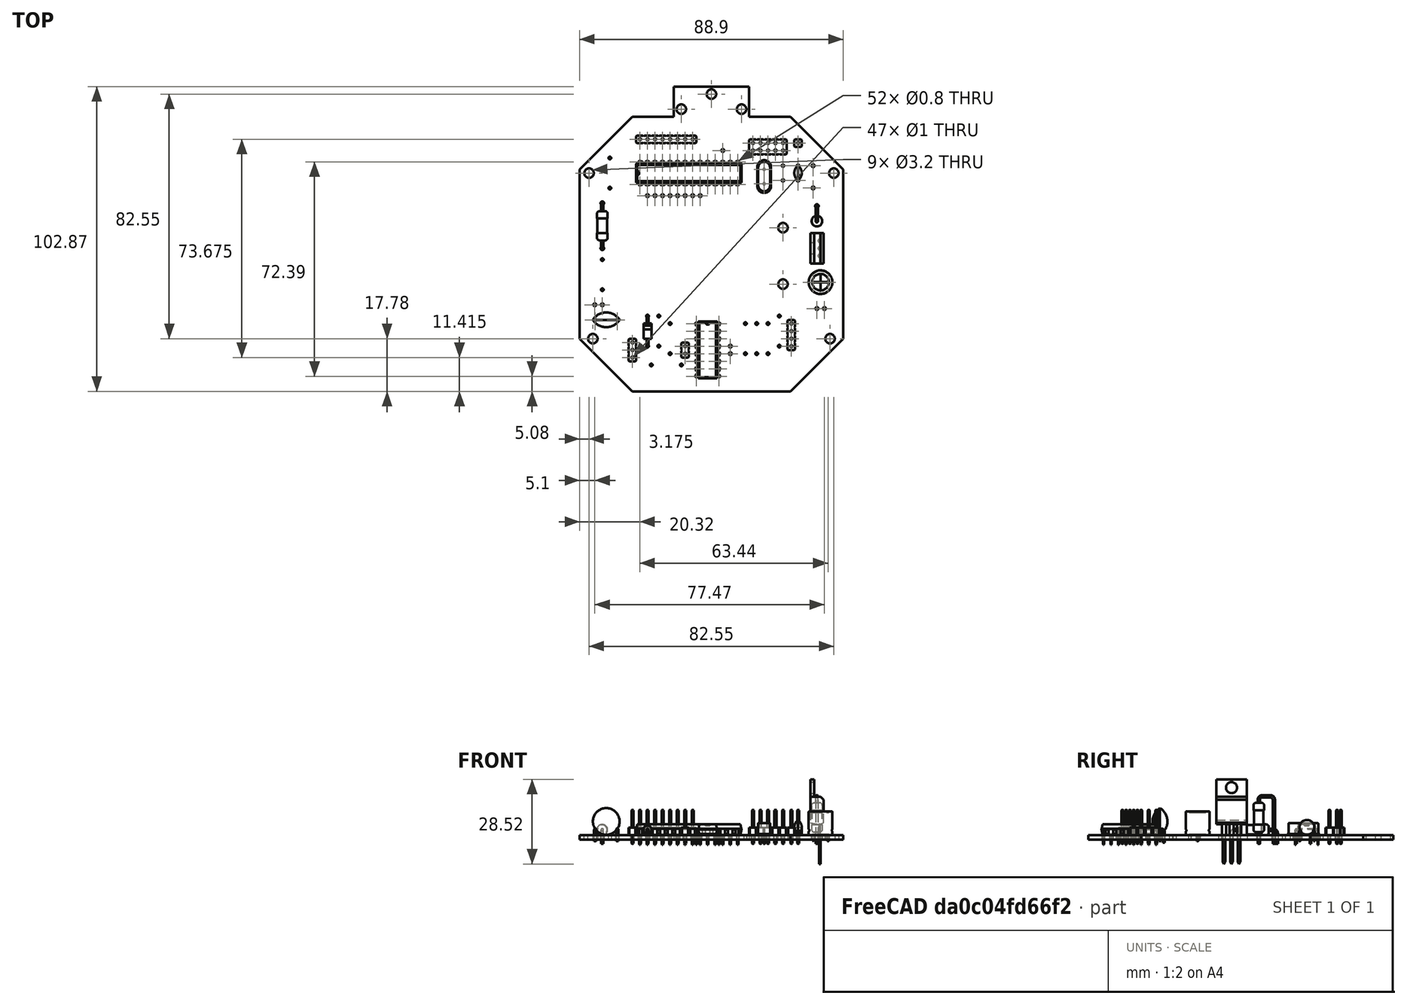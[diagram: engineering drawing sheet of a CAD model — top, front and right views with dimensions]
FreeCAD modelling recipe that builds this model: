
FCSTD DOCUMENT  (FreeCAD 0.21R33771 (Git))
Label: body
License: All rights reserved
LicenseURL: http://en.wikipedia.org/wiki/All_rights_reserved
objects: Part::Feature×20, App::Link×16, App::Part×4, PartDesign::CoordinateSystem×1, Sketcher::SketchObject×1
note: 22 computed .brp shape members not serialized (recipe doc carries the construction recipe); baked Part::Feature solids carry a one-line shape summary decoded from their .brp

FEATURE [PartDesign::CoordinateSystem] Local_CS_4a44
  AttacherType = Attacher::AttachEngine3D
  MapMode = 2
  Support = -> [X_Axis001]
FEATURE [Part::Feature] Pcb_4a44
  Placement = pos=(-114.3,114.3,0) rot=(0,0,1;0rad)
  shape: bbox 88.9 x 102.9 x 1.6 mm, 149 faces (baked)
FEATURE [Sketcher::SketchObject] PCB_Sketch_4a44
  FullyConstrained = false
  sketch-geometry (21):
    g0: LineSegment StartX=-12.7 StartY=48.26 StartZ=0 EndX=-12.7 EndY=58.42 EndZ=0
    g1: LineSegment StartX=-12.7 StartY=58.42 StartZ=0 EndX=12.7 EndY=58.42 EndZ=0
    g2: LineSegment StartX=12.7 StartY=58.42 StartZ=0 EndX=12.7 EndY=48.26 EndZ=0
    g3: LineSegment StartX=12.7 StartY=48.26 StartZ=0 EndX=26.67 EndY=48.26 EndZ=0
    g4: LineSegment StartX=26.67 StartY=48.26 StartZ=0 EndX=44.45 EndY=30.48 EndZ=0
    g5: LineSegment StartX=44.45 StartY=30.48 StartZ=0 EndX=44.45 EndY=-26.67 EndZ=0
    g6: LineSegment StartX=44.45 StartY=-26.67 StartZ=0 EndX=26.67 EndY=-44.45 EndZ=0
    g7: LineSegment StartX=26.67 StartY=-44.45 StartZ=0 EndX=-26.67 EndY=-44.45 EndZ=0
    g8: LineSegment StartX=-26.67 StartY=-44.45 StartZ=0 EndX=-44.45 EndY=-26.67 EndZ=0
    g9: LineSegment StartX=-44.45 StartY=-26.67 StartZ=0 EndX=-44.45 EndY=30.48 EndZ=0
    g10: LineSegment StartX=-44.45 StartY=30.48 StartZ=0 EndX=-26.67 EndY=48.26 EndZ=0
    g11: LineSegment StartX=-26.67 StartY=48.26 StartZ=0 EndX=-12.7 EndY=48.26 EndZ=0
    g12: Circle CenterX=41.275 CenterY=29.21 CenterZ=0 NormalX=0 NormalY=0 NormalZ=1 AngleXU=0 Radius=1.6
    g13: Circle CenterX=-41.275 CenterY=29.21 CenterZ=0 NormalX=0 NormalY=0 NormalZ=1 AngleXU=0 Radius=1.6
    g14: Circle CenterX=24.13 CenterY=10.795 CenterZ=0 NormalX=0 NormalY=0 NormalZ=1 AngleXU=0 Radius=1.6
    g15: Circle CenterX=10.16 CenterY=50.8 CenterZ=0 NormalX=0 NormalY=0 NormalZ=1 AngleXU=0 Radius=1.6
    g16: Circle CenterX=-10.16 CenterY=50.8 CenterZ=0 NormalX=0 NormalY=0 NormalZ=1 AngleXU=0 Radius=1.6
    g17: Circle CenterX=24.13 CenterY=-8.255 CenterZ=0 NormalX=0 NormalY=0 NormalZ=1 AngleXU=0 Radius=1.6
    g18: Circle CenterX=0 CenterY=55.88 CenterZ=0 NormalX=0 NormalY=0 NormalZ=1 AngleXU=0 Radius=1.6
    g19: Circle CenterX=-40.005 CenterY=-26.67 CenterZ=0 NormalX=0 NormalY=0 NormalZ=1 AngleXU=0 Radius=1.6
    g20: Circle CenterX=40.005 CenterY=-26.67 CenterZ=0 NormalX=0 NormalY=0 NormalZ=1 AngleXU=0 Radius=1.6
  constraints (12):
    c: Coincident(g8,g9)
    c: Coincident(g9,g10)
    c: Coincident(g7,g8)
    c: Coincident(g10,g11)
    c: Coincident(g0,g11)
    c: Coincident(g0,g1)
    c: Coincident(g2,g3)
    c: Coincident(g1,g2)
    c: Coincident(g6,g7)
    c: Coincident(g3,g4)
    c: Coincident(g5,g6)
    c: Coincident(g4,g5)
FEATURE [Part::Feature] Shape  label="schem.kicad_sch_D_A-405_P10.16mm_Horizontal_ddbd9ec53342"
  Placement = pos=(-21.57,-19.05,0) rot=(0,0,-1;1.5708rad)
  shape: bbox 2.72 x 10.91 x 5.71 mm, 15 faces (baked)
FEATURE [Part::Feature] Shape001  label="schem.kicad_sch_PinHeader_1x01_P254mm_Vertical_cfba1bc0ca3f"
  Placement = pos=(29.215,39.365,0) rot=(0,0,-1;1.5708rad)
  shape: bbox 2.54 x 2.54 x 11.54 mm, 28 faces (baked)
FEATURE [App::Link] schem_kicad_sch_D_A_405_P10_16mm_Horizontal_ddbd9ec53342_ln_  label="schem.kicad_sch_sch_D_A-405_P10.16mm_Horizontal_1a7e15e03997"
  LinkPlacement = pos=(-17.76,-29.21,0) rot=(0,0,1;1.5708rad)
  LinkedObject = -> Shape
  Placement = pos=(-17.76,-29.21,0) rot=(0,0,1;1.5708rad)
FEATURE [Part::Feature] Shape002  label="schem.kicad_sch_TO-220-3_Vertical_c42d6fc36a79"
  Placement = pos=(36.525,1.27,0) rot=(0,0,1;1.5708rad)
  shape: bbox 4.455 x 10.25 x 28.53 mm, 48 faces (baked)
FEATURE [App::Link] schem_kicad_sch_D_A_405_P10_16mm_Horizontal_ddbd9ec53342_ln_001  label="schem.kicad_sch_sch_D_A-405_P10.16mm_Horizontal_caf98be131d1"
  LinkPlacement = pos=(11.45,-21.59,0) rot=(0,0,-1;1.5708rad)
  LinkedObject = -> Shape
  Placement = pos=(11.45,-21.59,0) rot=(0,0,-1;1.5708rad)
FEATURE [Part::Feature] Shape003  label="schem.kicad_sch_PinHeader_1x03_P254mm_Vertical_ece9b4f67d39"
  Placement = pos=(-26.67,-27.955,0) rot=(0,0,1;0rad)
  shape: bbox 2.54 x 7.62 x 11.54 mm, 76 faces (baked)
FEATURE [Part::Feature] Shape004  label="schem.kicad_sch_R_Axial_DIN0411_L99mm_D36mm_P508mm_Vertical_02a39dee734d"
  Placement = pos=(35.58,13,0) rot=(0,0,1;1.5708rad)
  shape: bbox 3.897 x 7.56 x 16.63 mm, 17 faces (baked)
FEATURE [Part::Feature] Shape005  label="schem.kicad_sch_PinHeader_1x02_P254mm_Vertical_529c43ef1d2d"
  Placement = pos=(-8.87,-29.21,0) rot=(0,0,1;0rad)
  shape: bbox 2.54 x 5.08 x 11.54 mm, 52 faces (baked)
FEATURE [App::Link] schem_kicad_sch_PinHeader_1x02_P254mm_Vertical_529c43ef1d2d_ln_  label="schem.kicad_sch_sch_PinHeader_1x02_P254mm_Vertical_f29025659690"
  LinkPlacement = pos=(38.12,-16.51,0) rot=(0,0,-1;1.5708rad)
  LinkedObject = -> Shape005
  Placement = pos=(38.12,-16.51,0) rot=(0,0,-1;1.5708rad)
FEATURE [App::Link] schem_kicad_sch_D_A_405_P10_16mm_Horizontal_ddbd9ec53342_ln_002  label="schem.kicad_sch_sch_D_A-405_P10.16mm_Horizontal_2d3b61c36774"
  LinkPlacement = pos=(-36.81,0,0) rot=(0,0,-1;1.5708rad)
  LinkedObject = -> Shape
  Placement = pos=(-36.81,0,0) rot=(0,0,-1;1.5708rad)
FEATURE [App::Link] schem_kicad_sch_D_A_405_P10_16mm_Horizontal_ddbd9ec53342_ln_003  label="schem.kicad_sch_sch_D_A-405_P10.16mm_Horizontal_458fa9a440be"
  LinkPlacement = pos=(19.07,-21.59,0) rot=(0,0,-1;1.5708rad)
  LinkedObject = -> Shape
  Placement = pos=(19.07,-21.59,0) rot=(0,0,-1;1.5708rad)
FEATURE [Part::Feature] Shape006  label="schem.kicad_sch_DIP-16_W7.62mm_b1d0153299b9"
  Placement = pos=(-5.06,-21.59,0) rot=(0,0,1;0rad)
  shape: bbox 7.874 x 19.18 x 6.98 mm, 284 faces (baked)
FEATURE [App::Link] schem_kicad_sch_D_A_405_P10_16mm_Horizontal_ddbd9ec53342_ln_004  label="schem.kicad_sch_sch_D_A-405_P10.16mm_Horizontal_6ca63ce0451b"
  LinkPlacement = pos=(22.88,-29.21,0) rot=(0,0,1;1.5708rad)
  LinkedObject = -> Shape
  Placement = pos=(22.88,-29.21,0) rot=(0,0,1;1.5708rad)
FEATURE [Part::Feature] Shape007  label="schem.kicad_sch_C_Disc_D50mm_W25mm_P500mm_6b76e1a9cda5"
  Placement = pos=(29.21,31.75,0) rot=(0,0,-1;1.5708rad)
  shape: bbox 2.5 x 5.5 x 7.1 mm, 10 faces (baked)
FEATURE [App::Link] schem_kicad_sch_D_A_405_P10_16mm_Horizontal_ddbd9ec53342_ln_005  label="schem.kicad_sch_sch_D_A-405_P10.16mm_Horizontal_e68e0ba11600"
  LinkPlacement = pos=(-20.3,-35.56,0) rot=(0,0,1;0rad)
  LinkedObject = -> Shape
  Placement = pos=(-20.3,-35.56,0) rot=(0,0,1;0rad)
FEATURE [App::Link] schem_kicad_sch_D_A_405_P10_16mm_Horizontal_ddbd9ec53342_ln_006  label="schem.kicad_sch_sch_D_A-405_P10.16mm_Horizontal_b67de77c388f"
  LinkPlacement = pos=(-13.95,-31.75,0) rot=(0,0,1;1.5708rad)
  LinkedObject = -> Shape
  Placement = pos=(-13.95,-31.75,0) rot=(0,0,1;1.5708rad)
FEATURE [Part::Feature] Shape008  label="schem.kicad_sch_PinHeader_2x05_P254mm_Vertical_d3d50bb24435"
  Placement = pos=(24.13,39.37,0) rot=(0,0,-1;1.5708rad)
  shape: bbox 12.7 x 5.08 x 11.54 mm, 214 faces (baked)
FEATURE [App::Link] schem_kicad_sch_PinHeader_1x02_P254mm_Vertical_529c43ef1d2d_ln_001  label="schem.kicad_sch_sch_PinHeader_1x02_P254mm_Vertical_a67d2ab68a9a"
  LinkPlacement = pos=(6.37,-31.75,0) rot=(0,0,1;3.14159rad)
  LinkedObject = -> Shape005
  Placement = pos=(6.37,-31.75,0) rot=(0,0,1;3.14159rad)
FEATURE [Part::Feature] Shape009  label="schem.kicad_sch_PinHeader_1x08_P254mm_Vertical_d268c1571efe"
  Placement = pos=(-6.35,40.64,0) rot=(0,0,-1;1.5708rad)
  shape: bbox 20.32 x 2.54 x 11.54 mm, 196 faces (baked)
FEATURE [Part::Feature] Shape010  label="schem.kicad_sch_R_Axial_DIN0411_L99mm_D36mm_P1524mm_Horizontal_ddbd8a19e5c3"
  Placement = pos=(-36.81,3.81,0) rot=(0,0,1;1.5708rad)
  shape: bbox 3.897 x 16.3 x 6.748 mm, 17 faces (baked)
FEATURE [App::Link] schem_kicad_sch_D_A_405_P10_16mm_Horizontal_ddbd9ec53342_ln_007  label="schem.kicad_sch_sch_D_A-405_P10.16mm_Horizontal_d287fa47fda6"
  LinkPlacement = pos=(-34.27,24.13,0) rot=(0,0,1;1.5708rad)
  LinkedObject = -> Shape
  Placement = pos=(-34.27,24.13,0) rot=(0,0,1;1.5708rad)
FEATURE [Part::Feature] Shape011  label="schem.kicad_sch_C_Disc_D90mm_W50mm_P750mm_dadd0e61b2f0"
  Placement = pos=(-39.23,-20.32,0) rot=(0,0,1;0rad)
  shape: bbox 9 x 5 x 11.1 mm, 12 faces (baked)
FEATURE [Part::Feature] Shape012  label="schem.kicad_sch_PinHeader_1x04_P254mm_Vertical_2fe6705f866c"
  Placement = pos=(26.924,-21.59,0) rot=(0,0,1;0rad)
  shape: bbox 2.54 x 10.16 x 11.54 mm, 100 faces (baked)
FEATURE [App::Link] schem_kicad_sch_C_Disc_D90mm_W50mm_P750mm_dadd0e61b2f0_ln_  label="schem.kicad_sch_sch_C_Disc_D90mm_W50mm_P750mm_4acedab0acfc"
  LinkPlacement = pos=(34.31,31.69,0) rot=(0,0,-1;1.5708rad)
  LinkedObject = -> Shape011
  Placement = pos=(34.31,31.69,0) rot=(0,0,-1;1.5708rad)
FEATURE [App::Link] schem_kicad_sch_C_Disc_D50mm_W25mm_P500mm_6b76e1a9cda5_ln_  label="schem.kicad_sch_sch_C_Disc_D50mm_W25mm_P500mm_d71c322aaf49"
  LinkPlacement = pos=(24.13,31.71,0) rot=(0,0,-1;1.5708rad)
  LinkedObject = -> Shape007
  Placement = pos=(24.13,31.71,0) rot=(0,0,-1;1.5708rad)
FEATURE [Part::Feature] Shape013  label="schem.kicad_sch_Crystal_HC49-4H_Vertical_cb229fc18b84"
  Placement = pos=(17.78,30.48,0) rot=(0,0,-1;1.5708rad)
  shape: bbox 4.65 x 11.05 x 7 mm, 26 faces (baked)
FEATURE [App::Link] schem_kicad_sch_PinHeader_1x01_P254mm_Vertical_cfba1bc0ca3f_ln_  label="schem.kicad_sch_sch_PinHeader_1x01_P254mm_Vertical_37ca0bde1fe5"
  LinkPlacement = pos=(3.81,36.83,0) rot=(0,0,1;0rad)
  LinkedObject = -> Shape001
  Placement = pos=(3.81,36.83,0) rot=(0,0,1;0rad)
FEATURE [Part::Feature] Shape014  label="schem.kicad_sch_DIP-28_W7.62mm_d8168223c770"
  Placement = pos=(-24.13,25.4,0) rot=(0,0,1;1.5708rad)
  shape: bbox 35.56 x 7.874 x 6.98 mm, 488 faces (baked)
FEATURE [App::Link] schem_kicad_sch_D_A_405_P10_16mm_Horizontal_ddbd9ec53342_ln_008  label="schem.kicad_sch_sch_D_A-405_P10.16mm_Horizontal_8cfa2a53ac36"
  LinkPlacement = pos=(15.26,-31.75,0) rot=(0,0,1;1.5708rad)
  LinkedObject = -> Shape
  Placement = pos=(15.26,-31.75,0) rot=(0,0,1;1.5708rad)
FEATURE [App::Link] schem_kicad_sch_PinHeader_1x02_P254mm_Vertical_529c43ef1d2d_ln_002  label="schem.kicad_sch_sch_PinHeader_1x02_P254mm_Vertical_543f858bf19e"
  LinkPlacement = pos=(-39.35,-15.24,0) rot=(0,0,1;1.5708rad)
  LinkedObject = -> Shape005
  Placement = pos=(-39.35,-15.24,0) rot=(0,0,1;1.5708rad)
FEATURE [Part::Feature] Shape015  label="schem.kicad_sch_CP_Radial_D80mm_P500mm_4935b365757d"
  Placement = pos=(39.31,-7.62,0) rot=(0,0,1;3.14159rad)
  shape: bbox 9.886 x 10.23 x 10 mm, 54 faces (baked)
FEATURE [App::Link] schem_kicad_sch_PinHeader_1x08_P254mm_Vertical_d268c1571efe_ln_  label="schem.kicad_sch_sch_PinHeader_1x08_P254mm_Vertical_6abeb2a3ab84"
  LinkPlacement = pos=(-21.575,21.59,0) rot=(0,0,1;1.5708rad)
  LinkedObject = -> Shape009
  Placement = pos=(-21.575,21.59,0) rot=(0,0,1;1.5708rad)
FEATURE [App::Part] Top_4a44
  Group = -> [Shape,Shape001,schem_kicad_sch_D_A_405_P10_16mm_Horizontal_ddbd9ec53342_ln_,Shape002,schem_kicad_sch_D_A_405_P10_16mm_Horizontal_ddbd9ec53342_ln_001,Shape003,Shape004,Shape005,schem_kicad_sch_PinHeader_1x02_P254mm_Vertical_529c43ef1d2d_ln_,schem_kicad_sch_D_A_405_P10_16mm_Horizontal_ddbd9ec53342_ln_002,schem_kicad_sch_D_A_405_P10_16mm_Horizontal_ddbd9ec53342_ln_003,Shape006,+20 more]
  Origin = -> Origin003
FEATURE [App::Part] Step_Models_4a44
  Group = -> [Top_4a44]
  Origin = -> Origin002
FEATURE [Part::Feature] pads_area001  label="topPads_4a44"
  Placement = pos=(-114.3,114.3,0.02) rot=(0,0,1;0rad)
  shape: bbox 80.34 x 81.66 x 2e-07 mm, 126 faces, 0 solids (baked)
FEATURE [Part::Feature] Shape017  label="topTracks_4a44"
  Placement = pos=(-114.3,114.3,0.01) rot=(0,0,1;0rad)
  shape: bbox 82.88 x 89.23 x 2e-07 mm, 35 faces, 0 solids (baked)
FEATURE [Part::Feature] pads_area003  label="botPads_4a44"
  Placement = pos=(-114.3,114.3,-1.62) rot=(0,0,1;0rad)
  shape: bbox 80.34 x 81.66 x 2e-07 mm, 126 faces, 0 solids (baked)
FEATURE [App::Part] Board_Geoms_4a44
  Group = -> [Pcb_4a44,PCB_Sketch_4a44,pads_area001,Shape017,pads_area003]
  Origin = -> Origin
FEATURE [App::Part] Board_4a44  label="body"
  Group = -> [Local_CS_4a44,Board_Geoms_4a44,Step_Models_4a44]
  Origin = -> Origin001
